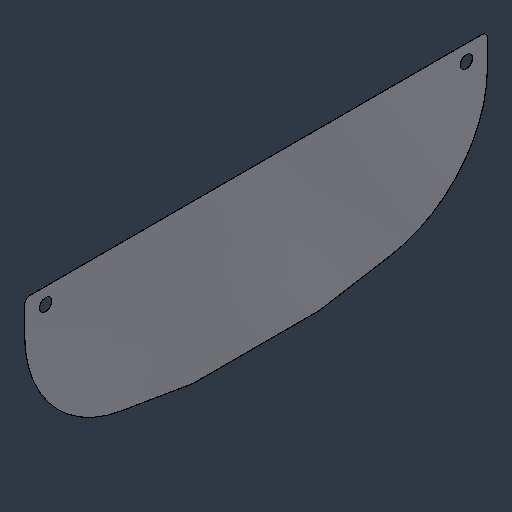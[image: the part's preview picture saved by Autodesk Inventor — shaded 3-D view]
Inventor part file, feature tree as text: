
AUTODESK INVENTOR PART (.ipt)
format: ipt  version: 2024.3 (Build 283343000, 343)  size: 91,648 bytes
history: native  units: mm (DEFAULTED — no unit token found)
features: fillet x1
ambient origin geometry x8: Origin, YZ Plane, XZ Plane, XY Plane, X Axis, Y Axis, Z Axis, Center Point
bodies: Solid1 (feature_tree)
feature tree (1):
  fillet  "Fillet1"  [1 undecoded]
note: 1 required parameter value undecoded (feature->parameter linkage not recoverable at this tier; creation-order binding heuristic only, values carry confidence <= 0.55)
